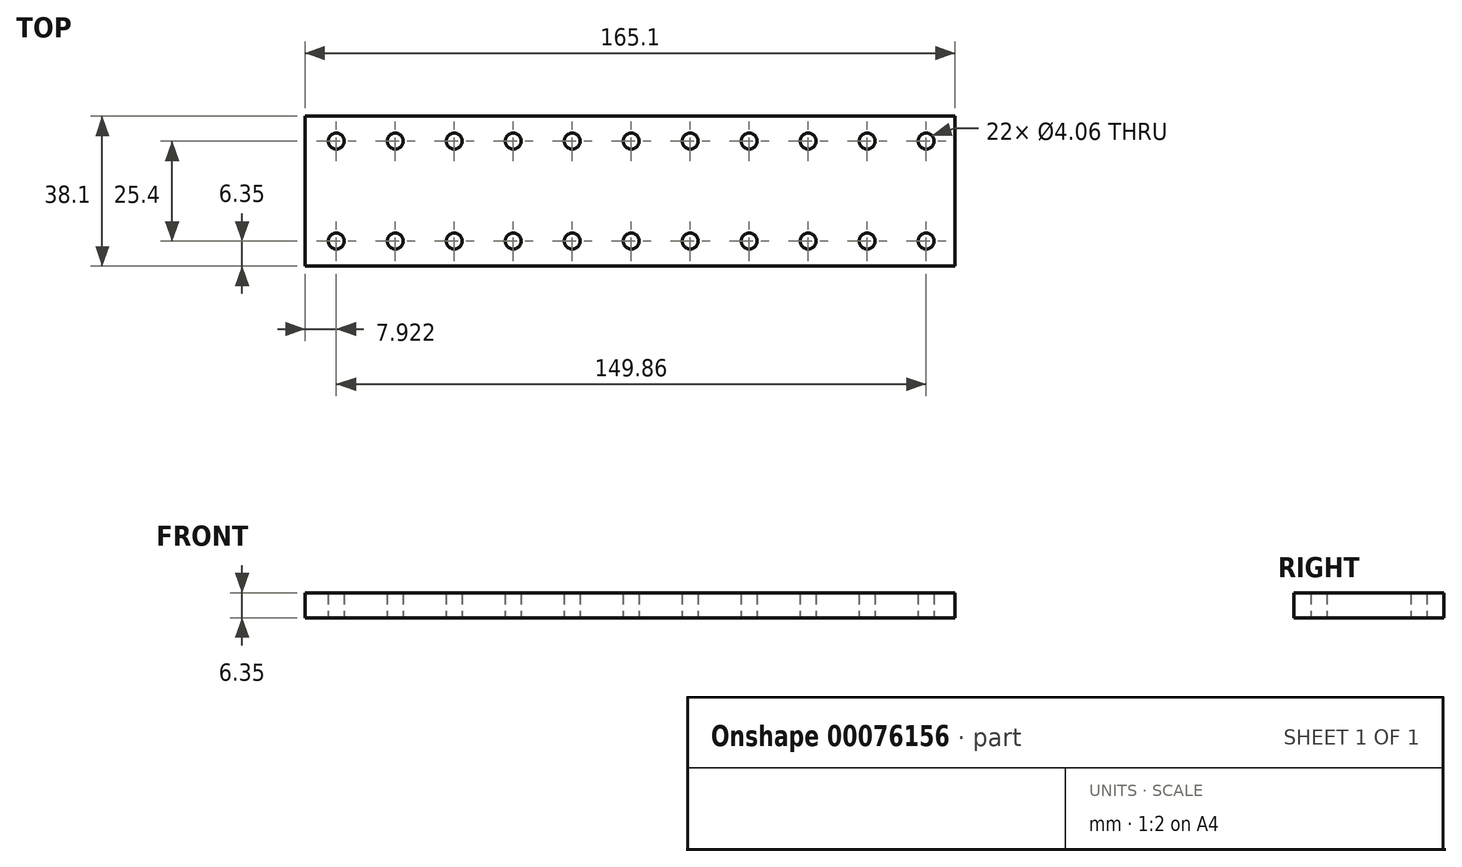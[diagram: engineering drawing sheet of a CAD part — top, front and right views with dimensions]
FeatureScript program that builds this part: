
annotation { "Feature Type Name" : "Feature", "Feature Type Description" : "" }
export const myFeature = defineFeature(function(context is Context, id is Id, definition is map)
    precondition{}
    {
        {
            var Q0;
            Q0=qCreatedBy(makeId("Top.planeOp"),FACE);
            var sketch = newSketch(context, id + "F0", { "sketchPlane" : qUnion([Q0])});
            skLineSegment(sketch, "E0.bottom", {"start": v(82.55, 19.05) * mm, "end": v(-82.55, 19.05) * mm});
            skLineSegment(sketch, "E0.top", {"start": v(82.55, -19.05) * mm, "end": v(-82.55, -19.05) * mm});
            skLineSegment(sketch, "E0.left", {"start": v(82.55, 19.05) * mm, "end": v(82.55, -19.05) * mm});
            skLineSegment(sketch, "E0.right", {"start": v(-82.55, 19.05) * mm, "end": v(-82.55, -19.05) * mm});
            skPoint(sketch, "E0.middle", {"position": v(0, 0) * mm});
            skLineSegment(sketch, "E1", {"start": v(-82.55, 12.7) * mm, "end": v(82.55, 12.7) * mm});
            skLineSegment(sketch, "E2", {"start": v(-82.55, -12.7) * mm, "end": v(82.55, -12.7) * mm});
            skCircle(sketch, "E3", {"center": v(-74.63, -12.7) * mm, "radius": 2.03 * mm});
            skCircle(sketch, "E4", {"center": v(-74.63, 12.7) * mm, "radius": 2.03 * mm});
            skCircle(sketch, "E5.1.0.0", {"center": v(-59.64, 12.7) * mm, "radius": 2.03 * mm});
            skCircle(sketch, "E5.1.0.1", {"center": v(-59.64, -12.7) * mm, "radius": 2.03 * mm});
            skCircle(sketch, "E5.2.0.0", {"center": v(-44.66, 12.7) * mm, "radius": 2.03 * mm});
            skCircle(sketch, "E5.2.0.1", {"center": v(-44.66, -12.7) * mm, "radius": 2.03 * mm});
            skCircle(sketch, "E5.3.0.0", {"center": v(-29.67, 12.7) * mm, "radius": 2.03 * mm});
            skCircle(sketch, "E5.3.0.1", {"center": v(-29.67, -12.7) * mm, "radius": 2.03 * mm});
            skCircle(sketch, "E5.4.0.0", {"center": v(-14.68, 12.7) * mm, "radius": 2.03 * mm});
            skCircle(sketch, "E5.4.0.1", {"center": v(-14.68, -12.7) * mm, "radius": 2.03 * mm});
            skCircle(sketch, "E5.5.0.0", {"center": v(0.3, 12.7) * mm, "radius": 2.03 * mm});
            skCircle(sketch, "E5.5.0.1", {"center": v(0.3, -12.7) * mm, "radius": 2.03 * mm});
            skCircle(sketch, "E5.6.0.0", {"center": v(15.29, 12.7) * mm, "radius": 2.03 * mm});
            skCircle(sketch, "E5.6.0.1", {"center": v(15.29, -12.7) * mm, "radius": 2.03 * mm});
            skCircle(sketch, "E5.7.0.0", {"center": v(30.27, 12.7) * mm, "radius": 2.03 * mm});
            skCircle(sketch, "E5.7.0.1", {"center": v(30.27, -12.7) * mm, "radius": 2.03 * mm});
            skCircle(sketch, "E5.8.0.0", {"center": v(45.26, 12.7) * mm, "radius": 2.03 * mm});
            skCircle(sketch, "E5.8.0.1", {"center": v(45.26, -12.7) * mm, "radius": 2.03 * mm});
            skCircle(sketch, "E5.9.0.0", {"center": v(60.25, 12.7) * mm, "radius": 2.03 * mm});
            skCircle(sketch, "E5.9.0.1", {"center": v(60.25, -12.7) * mm, "radius": 2.03 * mm});
            skCircle(sketch, "E5.10.0.0", {"center": v(75.23, 12.7) * mm, "radius": 2.03 * mm});
            skCircle(sketch, "E5.10.0.1", {"center": v(75.23, -12.7) * mm, "radius": 2.03 * mm});
            skLineSegment(sketch, "E5.direction1", {"start": v(-74.63, -12.7) * mm, "end": v(-59.64, -12.7) * mm, "construction": true});
            skSolve(sketch);
        }
        {
            var Q0;
            Q0 = qSketchRegion(id + "F0", true);
            extrude(context, id + "F1", {"entities" : qUnion([Q0]), "depth" : 6.35 * mm});
        }
    });
